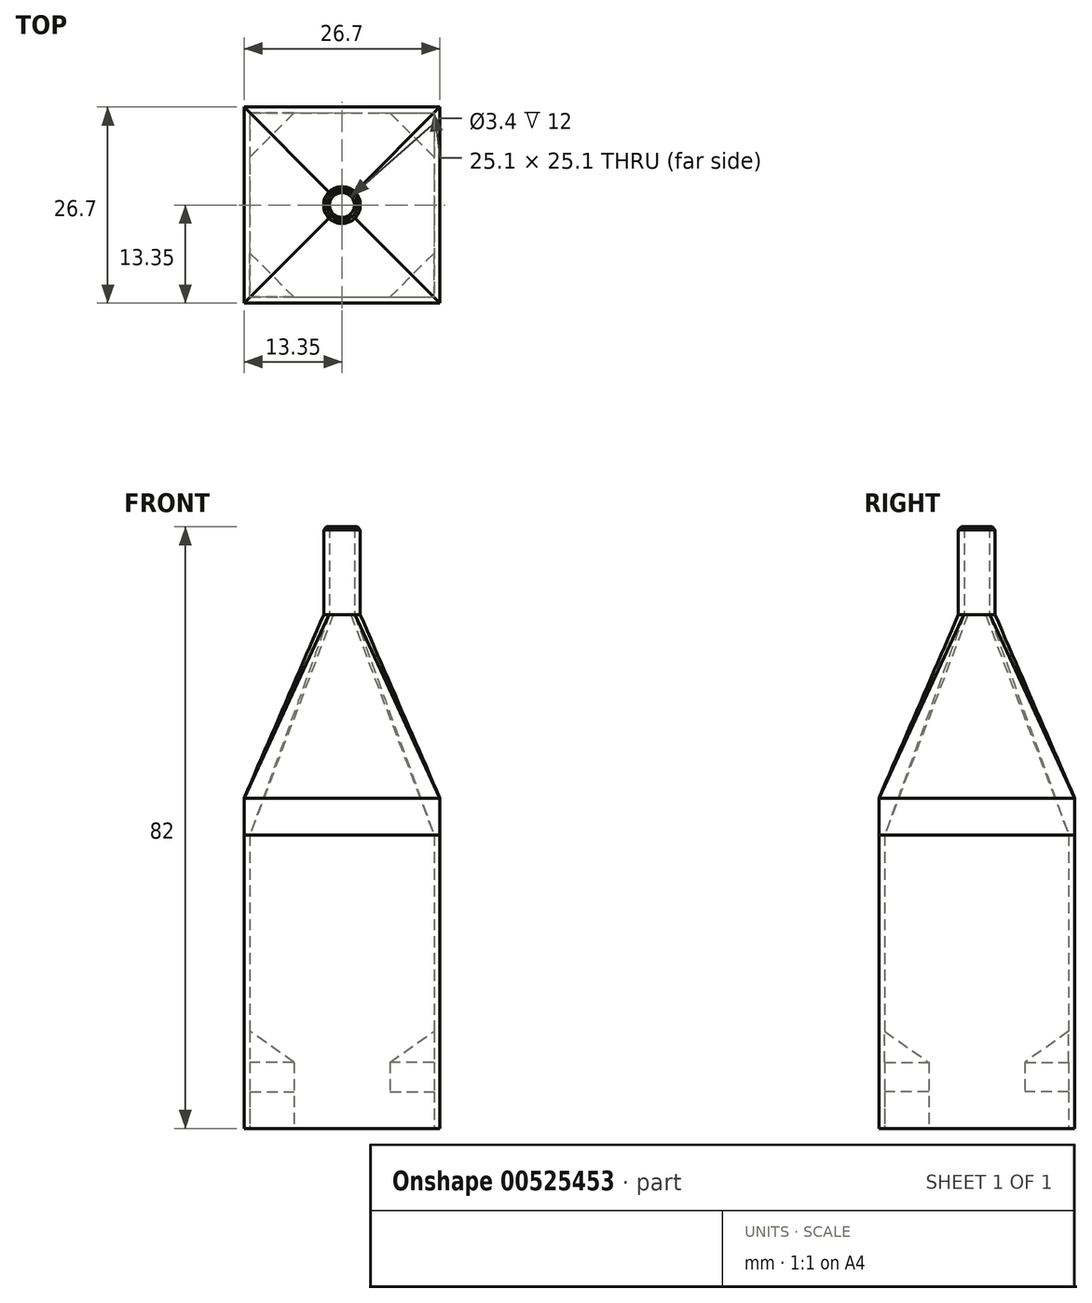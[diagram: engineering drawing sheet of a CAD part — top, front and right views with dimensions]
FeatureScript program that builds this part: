
annotation { "Feature Type Name" : "Feature", "Feature Type Description" : "" }
export const myFeature = defineFeature(function(context is Context, id is Id, definition is map)
    precondition{}
    {
        {
            var Q0;
            Q0=qCreatedBy(makeId("Top.planeOp"),FACE);
            var sketch = newSketch(context, id + "F0", { "sketchPlane" : qUnion([Q0])});
            skLineSegment(sketch, "E0.bottom", {"start": v(-12.55, 12.55) * mm, "end": v(12.55, 12.55) * mm});
            skLineSegment(sketch, "E0.top", {"start": v(-12.55, -12.55) * mm, "end": v(12.55, -12.55) * mm});
            skLineSegment(sketch, "E0.left", {"start": v(-12.55, 12.55) * mm, "end": v(-12.55, -12.55) * mm});
            skLineSegment(sketch, "E0.right", {"start": v(12.55, 12.55) * mm, "end": v(12.55, -12.55) * mm});
            skLineSegment(sketch, "E1.0", {"start": v(13.35, 13.35) * mm, "end": v(13.35, -13.35) * mm});
            skLineSegment(sketch, "E1.1", {"start": v(-13.35, 13.35) * mm, "end": v(13.35, 13.35) * mm});
            skLineSegment(sketch, "E1.2", {"start": v(-13.35, 13.35) * mm, "end": v(-13.35, -13.35) * mm});
            skLineSegment(sketch, "E1.3", {"start": v(-13.35, -13.35) * mm, "end": v(13.35, -13.35) * mm});
            skLineSegment(sketch, "E2", {"start": v(6.55, 12.55) * mm, "end": v(12.55, 6.55) * mm});
            skLineSegment(sketch, "E3.MirrorCS", {"start": v(-6.55, 12.55) * mm, "end": v(-12.55, 6.55) * mm});
            skLineSegment(sketch, "E4.MirrorCS", {"start": v(6.55, -12.55) * mm, "end": v(12.55, -6.55) * mm});
            skLineSegment(sketch, "E5.MirrorCS", {"start": v(-6.55, -12.55) * mm, "end": v(-12.55, -6.55) * mm});
            skSolve(sketch);
        }
        {
            var Q0;
            Q0=makeQuery(id+"F0.imprint","IMPRINT",FACE,{"disambiguationData":[TD([[makeQuery(id+"F0.imprint","IMPRINT",EDGE,{"derivedFrom":sQuery(id+"F0.wireOp",EDGE,"E1.0")}),-1.0]])]});
            extrude(context, id + "F1", {"entities" : qUnion([Q0]), "depth" : 40 * mm, "offsetDistance" : 25 * mm});
        }
        {
            var Q0;
            {var subQ3=sQuery(id+"F0.wireOp",EDGE,"E2");Q0=makeQuery(id+"F0.imprint","IMPRINT",FACE,{"disambiguationData":[TD([[makeQuery(id+"F0.imprint","IMPRINT",EDGE,{"derivedFrom":subQ3}),1.0]])]});}
            var Q1;
            {var subQ3=sQuery(id+"F0.wireOp",EDGE,"E3.MirrorCS");Q1=makeQuery(id+"F0.imprint","IMPRINT",FACE,{"disambiguationData":[TD([[makeQuery(id+"F0.imprint","IMPRINT",EDGE,{"derivedFrom":subQ3}),-1.0]])]});}
            var Q2;
            {var subQ3=sQuery(id+"F0.wireOp",EDGE,"E5.MirrorCS");Q2=makeQuery(id+"F0.imprint","IMPRINT",FACE,{"disambiguationData":[TD([[makeQuery(id+"F0.imprint","IMPRINT",EDGE,{"derivedFrom":subQ3}),1.0]])]});}
            var Q3;
            {var subQ3=sQuery(id+"F0.wireOp",EDGE,"E4.MirrorCS");Q3=makeQuery(id+"F0.imprint","IMPRINT",FACE,{"disambiguationData":[TD([[makeQuery(id+"F0.imprint","IMPRINT",EDGE,{"derivedFrom":subQ3}),-1.0]])]});}
            extrude(context, id + "F2", {"entities" : qUnion([Q0, Q1, Q2, Q3]), "operationType" : NewBodyOperationType.ADD, "depth" : 15 * mm, "offsetDistance" : 25 * mm});
        }
        {
            var Q0;
            {var subQ3=sQuery(id+"F0.wireOp",EDGE,"E2");Q0=makeQuery(id+"F0.imprint","IMPRINT",FACE,{"disambiguationData":[TD([[makeQuery(id+"F0.imprint","IMPRINT",EDGE,{"derivedFrom":subQ3}),1.0]])]});}
            var Q1;
            {var subQ3=sQuery(id+"F0.wireOp",EDGE,"E4.MirrorCS");Q1=makeQuery(id+"F0.imprint","IMPRINT",FACE,{"disambiguationData":[TD([[makeQuery(id+"F0.imprint","IMPRINT",EDGE,{"derivedFrom":subQ3}),-1.0]])]});}
            var Q2;
            {var subQ3=sQuery(id+"F0.wireOp",EDGE,"E3.MirrorCS");Q2=makeQuery(id+"F0.imprint","IMPRINT",FACE,{"disambiguationData":[TD([[makeQuery(id+"F0.imprint","IMPRINT",EDGE,{"derivedFrom":subQ3}),-1.0]])]});}
            extrude(context, id + "F3", {"entities" : qUnion([Q0, Q1, Q2]), "operationType" : NewBodyOperationType.REMOVE, "depth" : 5 * mm, "offsetDistance" : 25 * mm});
        }
        {
            var Q0;
            Q0=makeQuery(id+"F2.opExtrude","CAP_EDGE",EDGE,{"disambiguationData":[OSD([sQuery(id+"F0.wireOp",EDGE,"E2")])],"isStart":false});
            var Q1;
            Q1=makeQuery(id+"F2.opExtrude","CAP_EDGE",EDGE,{"disambiguationData":[OSD([sQuery(id+"F0.wireOp",EDGE,"E3.MirrorCS")])],"isStart":false});
            var Q2;
            Q2=makeQuery(id+"F2.opExtrude","CAP_EDGE",EDGE,{"disambiguationData":[OSD([sQuery(id+"F0.wireOp",EDGE,"E4.MirrorCS")])],"isStart":false});
            var Q3;
            Q3=makeQuery(id+"F2.opExtrude","CAP_EDGE",EDGE,{"disambiguationData":[OSD([sQuery(id+"F0.wireOp",EDGE,"E5.MirrorCS")])],"isStart":false});
            chamfer(context, id + "F4", {"entities" : qUnion([Q0, Q1, Q2, Q3]), "width" : 6 * mm, "tangentPropagation" : true});
        }
        {
            var Q0;
            Q0=qCreatedBy(makeId("Top.planeOp"),FACE);
            cPlane(context, id + "F5", {"entities" : qUnion([Q0]), "cplaneType" : CPlaneType.OFFSET, "offset" : 70 * mm, "width" : 150 * mm, "height" : 150 * mm});
        }
        {
            var Q0;
            Q0=qCreatedBy(id+"F5.planeOp",FACE);
            var sketch = newSketch(context, id + "F6", { "sketchPlane" : qUnion([Q0])});
            skCircle(sketch, "E6", {"center": v(0, 0) * mm, "radius": 2.5 * mm});
            skSolve(sketch);
        }
        {
            var Q0;
            Q0=makeQuery(id+"F1.opExtrude","CAP_FACE",FACE,{"disambiguationData":[OSD([sQuery(id+"F0.wireOp",EDGE,"E0.bottom"),sQuery(id+"F0.wireOp",EDGE,"E0.top"),sQuery(id+"F0.wireOp",EDGE,"E0.left"),sQuery(id+"F0.wireOp",EDGE,"E0.right"),sQuery(id+"F0.wireOp",EDGE,"E1.0"),sQuery(id+"F0.wireOp",EDGE,"E1.1"),sQuery(id+"F0.wireOp",EDGE,"E1.2"),sQuery(id+"F0.wireOp",EDGE,"E1.3")])],"isStart":false});
            var sketch = newSketch(context, id + "F7", { "sketchPlane" : qUnion([Q0])});
            skLineSegment(sketch, "E7", {"start": v(-13.35, 13.35) * mm, "end": v(13.35, 13.35) * mm});
            skLineSegment(sketch, "E8", {"start": v(13.35, 13.35) * mm, "end": v(13.35, -13.35) * mm});
            skLineSegment(sketch, "E9", {"start": v(13.35, -13.35) * mm, "end": v(-13.35, -13.35) * mm});
            skLineSegment(sketch, "E10", {"start": v(-13.35, -13.35) * mm, "end": v(-13.35, 13.35) * mm});
            skSolve(sketch);
        }
        {
            var Q0;
            Q0 = qSketchRegion(id + "F7", true);
            extrude(context, id + "F8", {"entities" : qUnion([Q0]), "depth" : 5 * mm, "offsetDistance" : 25 * mm});
        }
        {
            var Q1;
            Q1=makeQuery(id+"F6.imprint","IMPRINT",FACE,{"disambiguationData":[TD([[makeQuery(id+"F6.imprint","IMPRINT",EDGE,{"derivedFrom":sQuery(id+"F6.wireOp",EDGE,"E6")}),1.0]])]});
            var Q2;
            Q2=makeQuery(id+"F8.opExtrude","CAP_FACE",FACE,{"disambiguationData":[OSD([sQuery(id+"F7.wireOp",EDGE,"E7"),sQuery(id+"F7.wireOp",EDGE,"E8"),sQuery(id+"F7.wireOp",EDGE,"E9"),sQuery(id+"F7.wireOp",EDGE,"E10")])],"isStart":false});
            loft(context, id + "F9", {"operationType" : NewBodyOperationType.ADD, "sheetProfilesArray" : [{ "sheetProfileEntities" : qUnion([Q1]) }, { "sheetProfileEntities" : qUnion([Q2]) }]});
        }
        {
            var Q0;
            Q0=makeQuery(id+"F9.opLoft","CAP_FACE",FACE,{"disambiguationData":[OSD([makeQuery(id+"F6.imprint","IMPRINT",FACE,{"disambiguationData":[TD([[makeQuery(id+"F6.imprint","IMPRINT",EDGE,{"derivedFrom":sQuery(id+"F6.wireOp",EDGE,"E6")}),1.0]])]})])],"isStart":true});
            var sketch = newSketch(context, id + "F10", { "sketchPlane" : qUnion([Q0])});
            skCircle(sketch, "E11", {"center": v(0, 0) * mm, "radius": 1.7 * mm});
            skSolve(sketch);
        }
        {
            var Q0;
            Q0=makeQuery(id+"F10.imprint","IMPRINT",FACE,{"disambiguationData":[TD([[makeQuery(id+"F10.imprint","IMPRINT",EDGE,{"derivedFrom":sQuery(id+"F10.wireOp",EDGE,"E11")}),1.0]])]});
            var Q1;
            Q1=makeQuery(id+"F7.imprint","IMPRINT",FACE,{"disambiguationData":[TD([[makeQuery(id+"F7.imprint","IMPRINT",EDGE,{"derivedFrom":makeQuery(id+"F1.opExtrude","CAP_EDGE",EDGE,{"disambiguationData":[OSD([sQuery(id+"F0.wireOp",EDGE,"E0.bottom")])],"isStart":false})}),-1.0]])]});
            loft(context, id + "F11", {"operationType" : NewBodyOperationType.REMOVE, "sheetProfilesArray" : [{ "sheetProfileEntities" : qUnion([Q0]) }, { "sheetProfileEntities" : qUnion([Q1]) }]});
        }
        {
            var Q0;
            Q0=makeQuery(id+"F10.imprint","IMPRINT",FACE,{"disambiguationData":[TD([[makeQuery(id+"F10.imprint","IMPRINT",EDGE,{"derivedFrom":sQuery(id+"F10.wireOp",EDGE,"E11")}),-1.0]])]});
            extrude(context, id + "F12", {"entities" : qUnion([Q0]), "operationType" : NewBodyOperationType.ADD, "depth" : 12 * mm, "offsetDistance" : 25 * mm});
        }
        {
            var Q0;
            Q0=makeQuery(id+"F12.opExtrude","CAP_EDGE",EDGE,{"disambiguationData":[OSD([sQuery(id+"F6.wireOp",EDGE,"E6"),sQuery(id+"F7.wireOp",EDGE,"E7"),sQuery(id+"F7.wireOp",EDGE,"E8"),sQuery(id+"F7.wireOp",EDGE,"E9")])],"isStart":false});
            var Q1;
            Q1=makeQuery(id+"F12.opExtrude","CAP_EDGE",EDGE,{"disambiguationData":[OSD([sQuery(id+"F6.wireOp",EDGE,"E6"),sQuery(id+"F7.wireOp",EDGE,"E7"),sQuery(id+"F7.wireOp",EDGE,"E8")])],"isStart":false});
            var Q2;
            Q2=makeQuery(id+"F12.opExtrude","CAP_EDGE",EDGE,{"disambiguationData":[OSD([sQuery(id+"F6.wireOp",EDGE,"E6"),sQuery(id+"F7.wireOp",EDGE,"E7"),sQuery(id+"F7.wireOp",EDGE,"E8"),sQuery(id+"F7.wireOp",EDGE,"E9"),sQuery(id+"F7.wireOp",EDGE,"E10")])],"isStart":false});
            var Q3;
            Q3=makeQuery(id+"F12.opExtrude","CAP_EDGE",EDGE,{"disambiguationData":[OSD([sQuery(id+"F6.wireOp",EDGE,"E6"),sQuery(id+"F7.wireOp",EDGE,"E8"),sQuery(id+"F7.wireOp",EDGE,"E9"),sQuery(id+"F7.wireOp",EDGE,"E10")])],"isStart":false});
            chamfer(context, id + "F13", {"entities" : qUnion([Q0, Q1, Q2, Q3]), "width" : 0.4 * mm, "tangentPropagation" : true});
        }
    });
